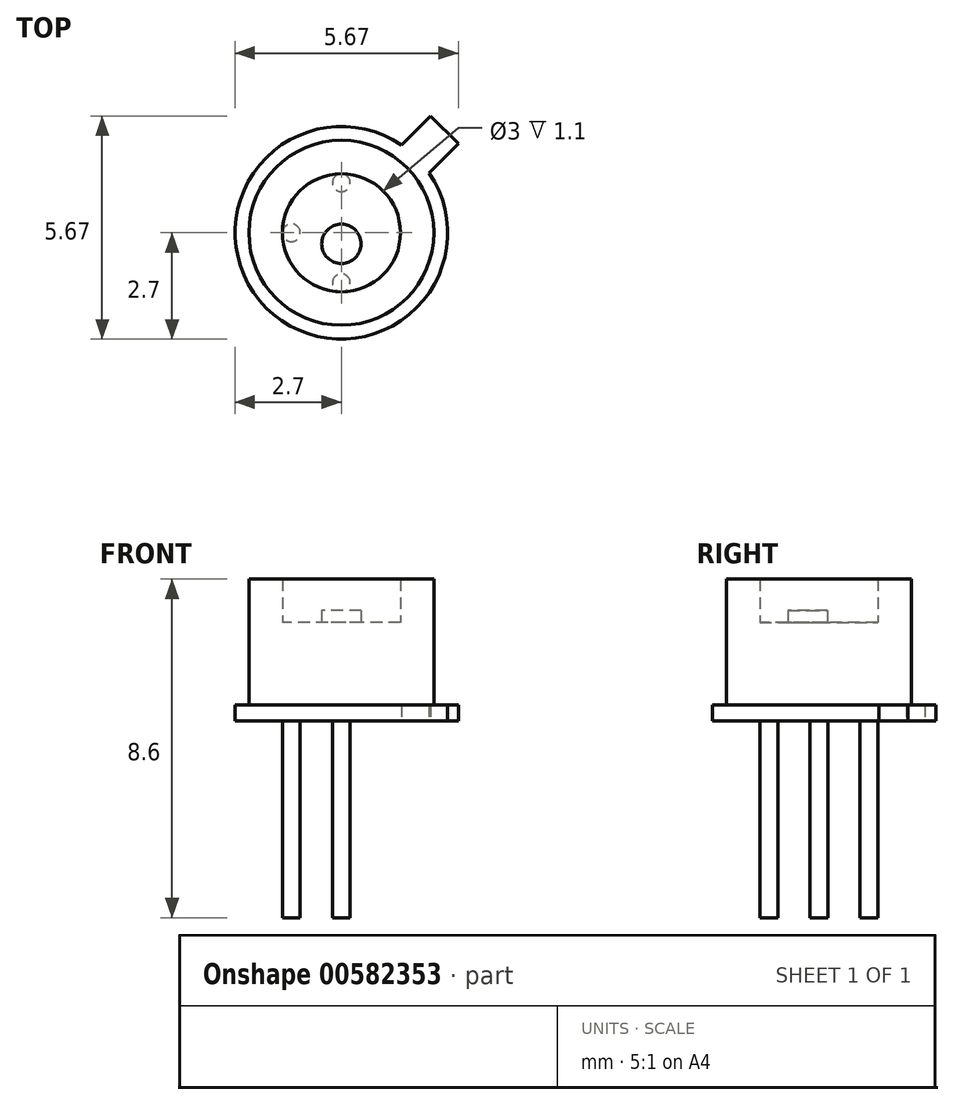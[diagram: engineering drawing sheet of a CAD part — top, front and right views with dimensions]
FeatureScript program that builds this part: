
annotation { "Feature Type Name" : "Feature", "Feature Type Description" : "" }
export const myFeature = defineFeature(function(context is Context, id is Id, definition is map)
    precondition{}
    {
        {
            var Q0;
            Q0=qCreatedBy(makeId("Top.planeOp"),FACE);
            var sketch = newSketch(context, id + "F0", { "sketchPlane" : qUnion([Q0])});
            skArc(sketch, "E0", {"start": v(1.52, 2.23) * mm, "mid": v(-1.9, -1.9) * mm, "end": v(2.23, 1.52) * mm});
            skCircle(sketch, "E1", {"center": v(0, 0) * mm, "radius": 2.35 * mm});
            skCircle(sketch, "E2", {"center": v(0, 0) * mm, "radius": 1.5 * mm});
            skCircle(sketch, "E3", {"center": v(0, 0) * mm, "radius": 1.27 * mm, "construction": true});
            skLineSegment(sketch, "E4", {"start": v(0, 0) * mm, "end": v(3.7, 0) * mm, "construction": true});
            skLineSegment(sketch, "E5", {"start": v(0, 0) * mm, "end": v(2.62, 2.62) * mm, "construction": true});
            skLineSegment(sketch, "E6", {"start": v(2.62, 2.62) * mm, "end": v(2.97, 2.26) * mm});
            skLineSegment(sketch, "E7", {"start": v(2.97, 2.26) * mm, "end": v(2.23, 1.52) * mm});
            skLineSegment(sketch, "E8", {"start": v(2.62, 2.62) * mm, "end": v(2.26, 2.97) * mm});
            skLineSegment(sketch, "E9", {"start": v(2.26, 2.97) * mm, "end": v(1.52, 2.23) * mm});
            skLineSegment(sketch, "E10", {"start": v(0, 0) * mm, "end": v(-2.7, 0) * mm, "construction": true});
            skLineSegment(sketch, "E11", {"start": v(0, 2.7) * mm, "end": v(0, -2.7) * mm, "construction": true});
            skSolve(sketch);
        }
        {
            var Q0;
            Q0=makeQuery(id+"F0.imprint","IMPRINT",FACE,{"disambiguationData":[TD([[makeQuery(id+"F0.imprint","IMPRINT",EDGE,{"derivedFrom":sQuery(id+"F0.wireOp",EDGE,"E1")}),1.0]])]});
            extrude(context, id + "F1", {"entities" : qUnion([Q0]), "depth" : 3.6 * mm, "offsetDistance" : 25 * mm});
        }
        {
            var Q0;
            Q0=makeQuery(id+"F0.imprint","IMPRINT",FACE,{"disambiguationData":[TD([[makeQuery(id+"F0.imprint","IMPRINT",EDGE,{"derivedFrom":sQuery(id+"F0.wireOp",EDGE,"E0")}),1.0]])]});
            extrude(context, id + "F2", {"entities" : qUnion([Q0]), "operationType" : NewBodyOperationType.ADD, "depth" : 0.4 * mm, "offsetDistance" : 25 * mm});
        }
        {
            var Q0;
            Q0=makeQuery(id+"F0.imprint","IMPRINT",FACE,{"disambiguationData":[TD([[makeQuery(id+"F0.imprint","IMPRINT",EDGE,{"derivedFrom":sQuery(id+"F0.wireOp",EDGE,"E2")}),1.0]])]});
            extrude(context, id + "F3", {"entities" : qUnion([Q0]), "operationType" : NewBodyOperationType.ADD, "depth" : 2.5 * mm, "offsetDistance" : 25 * mm});
        }
        {
            var Q0;
            Q0=makeQuery(id+"F3.opExtrude","CAP_FACE",FACE,{"disambiguationData":[OSD([sQuery(id+"F0.wireOp",EDGE,"E2")])],"isStart":false});
            var sketch = newSketch(context, id + "F4", { "sketchPlane" : qUnion([Q0])});
            skCircle(sketch, "E12", {"center": v(0, -0.28) * mm, "radius": 0.5 * mm});
            skSolve(sketch);
        }
        {
            var Q0;
            Q0=makeQuery(id+"F4.imprint","IMPRINT",FACE,{"disambiguationData":[TD([[makeQuery(id+"F4.imprint","IMPRINT",EDGE,{"derivedFrom":sQuery(id+"F4.wireOp",EDGE,"E12")}),1.0]])]});
            extrude(context, id + "F5", {"entities" : qUnion([Q0]), "operationType" : NewBodyOperationType.ADD, "depth" : 0.3 * mm, "offsetDistance" : 25 * mm});
        }
        {
            var Q0;
            Q0=makeQuery(id+"F0.imprint","IMPRINT",FACE,{"disambiguationData":[TD([[makeQuery(id+"F0.imprint","IMPRINT",EDGE,{"derivedFrom":sQuery(id+"F0.wireOp",EDGE,"E2")}),1.0]])]});
            var sketch = newSketch(context, id + "F6", { "sketchPlane" : qUnion([Q0])});
            skCircle(sketch, "E13.0", {"center": v(0, 0) * mm, "radius": 1.27 * mm, "construction": true});
            skLineSegment(sketch, "E14.0", {"start": v(0, 2.7) * mm, "end": v(0, -2.7) * mm, "construction": true});
            skLineSegment(sketch, "E15.0", {"start": v(0, 0) * mm, "end": v(3.7, 0) * mm, "construction": true});
            skLineSegment(sketch, "E16.0", {"start": v(0, 0) * mm, "end": v(-2.7, 0) * mm, "construction": true});
            skCircle(sketch, "E17", {"center": v(-1.27, 0) * mm, "radius": 0.23 * mm});
            skCircle(sketch, "E18", {"center": v(0, 1.27) * mm, "radius": 0.23 * mm});
            skCircle(sketch, "E19", {"center": v(0, -1.27) * mm, "radius": 0.23 * mm});
            skSolve(sketch);
        }
        {
            var Q0;
            Q0=makeQuery(id+"F6.imprint","IMPRINT",FACE,{"disambiguationData":[TD([[makeQuery(id+"F6.imprint","IMPRINT",EDGE,{"derivedFrom":sQuery(id+"F6.wireOp",EDGE,"E19")}),1.0]])]});
            var Q1;
            Q1=makeQuery(id+"F6.imprint","IMPRINT",FACE,{"disambiguationData":[TD([[makeQuery(id+"F6.imprint","IMPRINT",EDGE,{"derivedFrom":sQuery(id+"F6.wireOp",EDGE,"E17")}),1.0]])]});
            var Q2;
            Q2=makeQuery(id+"F6.imprint","IMPRINT",FACE,{"disambiguationData":[TD([[makeQuery(id+"F6.imprint","IMPRINT",EDGE,{"derivedFrom":sQuery(id+"F6.wireOp",EDGE,"E18")}),1.0]])]});
            extrude(context, id + "F7", {"entities" : qUnion([Q0, Q1, Q2]), "operationType" : NewBodyOperationType.ADD, "oppositeDirection" : true, "depth" : 5 * mm, "offsetDistance" : 25 * mm});
        }
    });
